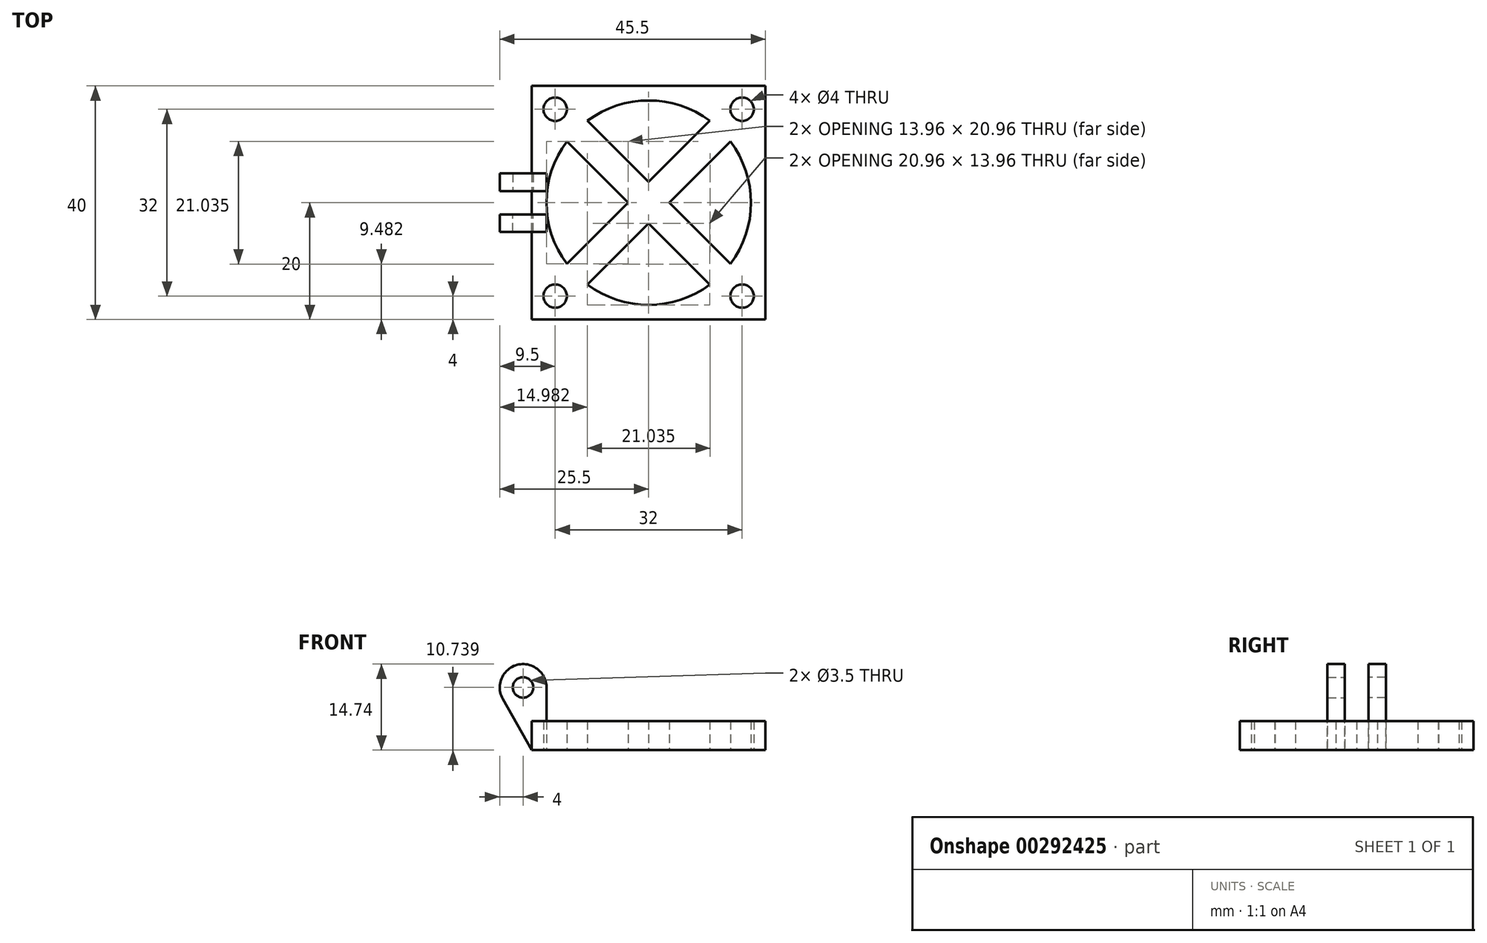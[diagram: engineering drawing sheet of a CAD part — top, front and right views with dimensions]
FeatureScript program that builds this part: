
annotation { "Feature Type Name" : "Feature", "Feature Type Description" : "" }
export const myFeature = defineFeature(function(context is Context, id is Id, definition is map)
    precondition{}
    {
        {
            var Q0;
            Q0=qCreatedBy(makeId("Top.planeOp"),FACE);
            var sketch = newSketch(context, id + "F0", { "sketchPlane" : qUnion([Q0])});
            skLineSegment(sketch, "E0.bottom", {"start": v(0, 0) * mm, "end": v(40, 0) * mm});
            skLineSegment(sketch, "E0.top", {"start": v(0, 40) * mm, "end": v(40, 40) * mm});
            skLineSegment(sketch, "E0.left", {"start": v(0, 0) * mm, "end": v(0, 40) * mm});
            skLineSegment(sketch, "E0.right", {"start": v(40, 0) * mm, "end": v(40, 40) * mm});
            skArc(sketch, "E1", {"start": v(5.98, 30.48) * mm, "mid": v(2.5, 20) * mm, "end": v(5.98, 9.52) * mm});
            skPoint(sketch, "E1.centerSnap0", {"position": v(40, 20) * mm});
            skPoint(sketch, "E1.centerSnap1", {"position": v(20, 40) * mm});
            skLineSegment(sketch, "E2", {"start": v(5.98, 9.52) * mm, "end": v(16.46, 20) * mm});
            skLineSegment(sketch, "E3", {"start": v(9.52, 5.98) * mm, "end": v(20, 16.46) * mm});
            skLineSegment(sketch, "E4", {"start": v(30.48, 5.98) * mm, "end": v(20, 16.46) * mm});
            skLineSegment(sketch, "E5", {"start": v(34.02, 9.52) * mm, "end": v(23.54, 20) * mm});
            skLineSegment(sketch, "E6.trimOffspring", {"start": v(20, 23.54) * mm, "end": v(30.48, 34.02) * mm});
            skLineSegment(sketch, "E7.trimOffspring", {"start": v(23.54, 20) * mm, "end": v(34.02, 30.48) * mm});
            skLineSegment(sketch, "E8.trimOffspring", {"start": v(16.46, 20) * mm, "end": v(5.98, 30.48) * mm});
            skLineSegment(sketch, "E9.trimOffspring", {"start": v(20, 23.54) * mm, "end": v(9.52, 34.02) * mm});
            skArc(sketch, "E10.trimOffspring", {"start": v(30.48, 34.02) * mm, "mid": v(20, 37.5) * mm, "end": v(9.52, 34.02) * mm});
            skArc(sketch, "E11.trimOffspring", {"start": v(34.02, 9.52) * mm, "mid": v(37.5, 20) * mm, "end": v(34.02, 30.48) * mm});
            skArc(sketch, "E12.trimOffspring", {"start": v(9.52, 5.98) * mm, "mid": v(20, 2.5) * mm, "end": v(30.48, 5.98) * mm});
            skCircle(sketch, "E13", {"center": v(4, 36) * mm, "radius": 2 * mm});
            skCircle(sketch, "E14", {"center": v(36, 36) * mm, "radius": 2 * mm});
            skCircle(sketch, "E15", {"center": v(36, 4) * mm, "radius": 2 * mm});
            skCircle(sketch, "E16", {"center": v(4, 4) * mm, "radius": 2 * mm});
            skSolve(sketch);
        }
        {
            var Q0;
            Q0 = qSketchRegion(id + "F0", true);
            extrude(context, id + "F1", {"entities" : qUnion([Q0]), "depth" : 5 * mm});
        }
        {
            var Q0;
            Q0=makeQuery(id+"F1.opExtrude","SWEPT_FACE",FACE,{"disambiguationData":[OSD([sQuery(id+"F0.wireOp",EDGE,"E0.bottom")])]});
            cPlane(context, id + "F2", {"entities" : qUnion([Q0]), "cplaneType" : CPlaneType.OFFSET, "offset" : 22 * mm, "oppositeDirection" : true, "width" : 150 * mm, "height" : 150 * mm});
        }
        {
            var Q0;
            Q0=qCreatedBy(id+"F2.planeOp",FACE);
            var sketch = newSketch(context, id + "F3", { "sketchPlane" : qUnion([Q0])});
            skArc(sketch, "E17", {"start": v(2.5, 10.74) * mm, "mid": v(-2.52, 14.6) * mm, "end": v(-4.98, 8.76) * mm});
            skCircle(sketch, "E18", {"center": v(-1.5, 10.74) * mm, "radius": 1.75 * mm});
            skLineSegment(sketch, "E19", {"start": v(0, 0) * mm, "end": v(-4.98, 8.76) * mm});
            skLineSegment(sketch, "E20", {"start": v(2.5, 0) * mm, "end": v(2.5, 5) * mm, "construction": true});
            skLineSegment(sketch, "E21", {"start": v(2.5, 5) * mm, "end": v(2.5, 10.74) * mm});
            skLineSegment(sketch, "E22.0", {"start": v(0, 5) * mm, "end": v(2.5, 5) * mm});
            skLineSegment(sketch, "E23.0", {"start": v(0, 5) * mm, "end": v(0, 0) * mm});
            skPoint(sketch, "E24.orphan", {"position": v(40, 5) * mm});
            skSolve(sketch);
        }
        {
            var Q0;
            Q0 = qSketchRegion(id + "F3", true);
            extrude(context, id + "F4", {"entities" : qUnion([Q0]), "operationType" : NewBodyOperationType.ADD, "oppositeDirection" : true, "depth" : 3 * mm});
        }
        {
            var Q0;
            Q0=qCreatedBy(id+"F2.planeOp",FACE);
            cPlane(context, id + "F5", {"entities" : qUnion([Q0]), "cplaneType" : CPlaneType.OFFSET, "offset" : 4 * mm, "width" : 150 * mm, "height" : 150 * mm});
        }
        {
            var Q0;
            Q0=qCreatedBy(id+"F5.planeOp",FACE);
            var sketch = newSketch(context, id + "F6", { "sketchPlane" : qUnion([Q0])});
            skLineSegment(sketch, "E25.0.0", {"start": v(0, 0) * mm, "end": v(0, 5) * mm});
            skLineSegment(sketch, "E25.0.1", {"start": v(0, 5) * mm, "end": v(2.5, 5) * mm});
            skLineSegment(sketch, "E25.0.2", {"start": v(2.5, 5) * mm, "end": v(2.5, 10.74) * mm});
            skArc(sketch, "E25.0.3", {"start": v(2.5, 10.74) * mm, "mid": v(-2.52, 14.6) * mm, "end": v(-4.98, 8.76) * mm});
            skLineSegment(sketch, "E25.0.4", {"start": v(-4.98, 8.76) * mm, "end": v(0, 0) * mm});
            skCircle(sketch, "E26.0", {"center": v(-1.5, 10.74) * mm, "radius": 1.75 * mm});
            skSolve(sketch);
        }
        {
            var Q0;
            Q0 = qSketchRegion(id + "F6", true);
            extrude(context, id + "F7", {"entities" : qUnion([Q0]), "operationType" : NewBodyOperationType.ADD, "depth" : 3 * mm});
        }
    });
